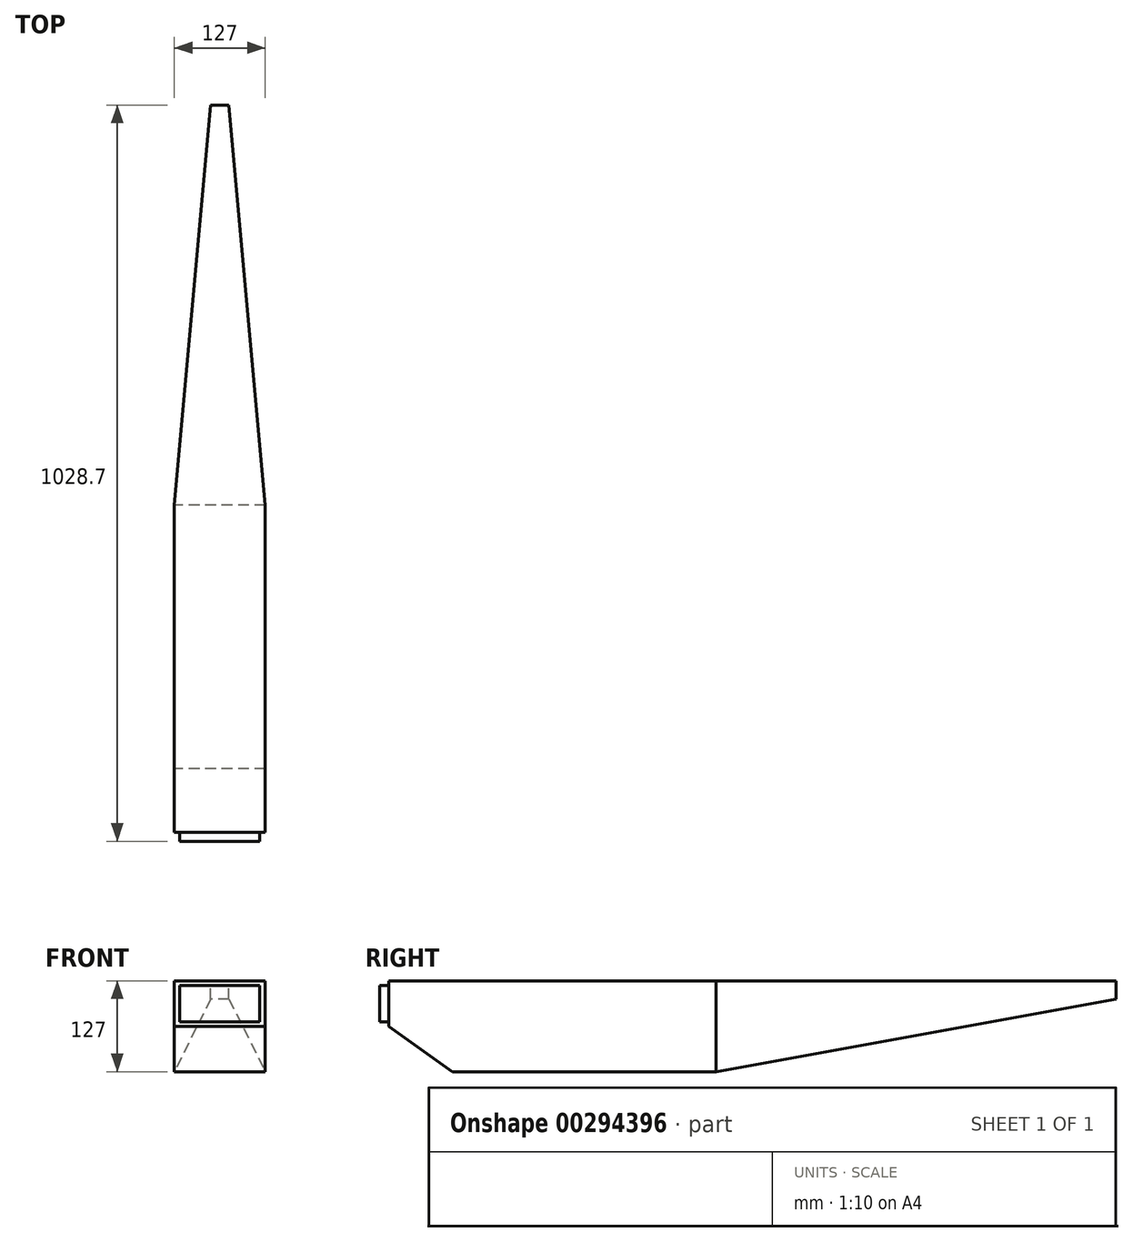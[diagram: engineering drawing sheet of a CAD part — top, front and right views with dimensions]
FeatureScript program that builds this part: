
annotation { "Feature Type Name" : "Feature", "Feature Type Description" : "" }
export const myFeature = defineFeature(function(context is Context, id is Id, definition is map)
    precondition{}
    {
        {
            var Q0;
            Q0=qCreatedBy(makeId("Right.planeOp"),FACE);
            var sketch = newSketch(context, id + "F0", { "sketchPlane" : qUnion([Q0])});
            skLineSegment(sketch, "E0.bottom", {"start": v(-949.91, 104.8) * mm, "end": v(66.09, 104.8) * mm});
            skLineSegment(sketch, "E0.top", {"start": v(-861.01, -22.2) * mm, "end": v(-492.71, -22.2) * mm});
            skLineSegment(sketch, "E0.left", {"start": v(-949.91, 104.8) * mm, "end": v(-949.91, 41.3) * mm});
            skLineSegment(sketch, "E0.right", {"start": v(66.09, 104.8) * mm, "end": v(66.09, 79.4) * mm});
            skPoint(sketch, "E1", {"position": v(66.09, 79.4) * mm});
            skPoint(sketch, "E2", {"position": v(-492.71, -22.2) * mm});
            skLineSegment(sketch, "E3", {"start": v(-492.71, -22.2) * mm, "end": v(66.09, 79.4) * mm});
            skPoint(sketch, "E4.orphan", {"position": v(66.09, -22.2) * mm});
            skPoint(sketch, "E5", {"position": v(-861.01, -22.2) * mm});
            skLineSegment(sketch, "E6", {"start": v(-949.91, 41.3) * mm, "end": v(-861.01, -22.2) * mm});
            skPoint(sketch, "E7.orphan", {"position": v(-949.91, -22.2) * mm});
            skSolve(sketch);
        }
        {
            var Q0;
            Q0 = qSketchRegion(id + "F0", true);
            extrude(context, id + "F1", {"entities" : qUnion([Q0]), "depth" : 127 * mm, "offsetDistance" : 25.4 * mm});
        }
        {
            var Q0;
            Q0=makeQuery(id+"F1.opExtrude","SWEPT_FACE",FACE,{"disambiguationData":[OSD([sQuery(id+"F0.wireOp",EDGE,"E0.left")])]});
            var sketch = newSketch(context, id + "F2", { "sketchPlane" : qUnion([Q0])});
            skLineSegment(sketch, "E8.bottom", {"start": v(7.4, 98.44) * mm, "end": v(119.16, 98.44) * mm});
            skLineSegment(sketch, "E8.top", {"start": v(7.4, 47.64) * mm, "end": v(119.16, 47.64) * mm});
            skLineSegment(sketch, "E8.left", {"start": v(7.4, 98.44) * mm, "end": v(7.4, 47.64) * mm});
            skLineSegment(sketch, "E8.right", {"start": v(119.16, 98.44) * mm, "end": v(119.16, 47.64) * mm});
            skSolve(sketch);
        }
        {
            var Q0;
            Q0 = qSketchRegion(id + "F2", true);
            extrude(context, id + "F3", {"entities" : qUnion([Q0]), "operationType" : NewBodyOperationType.ADD, "depth" : 12.7 * mm, "offsetDistance" : 25.4 * mm});
        }
        {
            var Q0;
            Q0=makeQuery(id+"F1.opExtrude","SWEPT_FACE",FACE,{"disambiguationData":[OSD([sQuery(id+"F0.wireOp",EDGE,"E0.bottom")])]});
            var sketch = newSketch(context, id + "F4", { "sketchPlane" : qUnion([Q0])});
            skPoint(sketch, "E9", {"position": v(127, -492.71) * mm});
            skPoint(sketch, "E10", {"position": v(63.5, 66.09) * mm});
            skPoint(sketch, "E11", {"position": v(76.2, 66.09) * mm});
            skPoint(sketch, "E12", {"position": v(50.8, 66.09) * mm});
            skPoint(sketch, "E13", {"position": v(0, -492.71) * mm});
            skLineSegment(sketch, "E14", {"start": v(50.8, 66.09) * mm, "end": v(0, -492.71) * mm});
            skLineSegment(sketch, "E15", {"start": v(76.2, 66.09) * mm, "end": v(127, -492.71) * mm});
            skLineSegment(sketch, "E16", {"start": v(127, 66.09) * mm, "end": v(76.2, 66.09) * mm});
            skLineSegment(sketch, "E17", {"start": v(0, 66.09) * mm, "end": v(0, -492.71) * mm});
            skLineSegment(sketch, "E18.trimOffspring", {"start": v(50.8, 66.09) * mm, "end": v(0, 66.09) * mm});
            skSolve(sketch);
        }
        {
            var Q0;
            Q0=makeQuery(id+"F4.imprint","IMPRINT",FACE,{"disambiguationData":[TD([[makeQuery(id+"F4.imprint","IMPRINT",EDGE,{"derivedFrom":sQuery(id+"F4.wireOp",EDGE,"E14")}),-1.0]])]});
            var Q1;
            {var subQ0=sQuery(id+"F4.wireOp",EDGE,"E15");Q1=makeQuery(id+"F4.imprint","IMPRINT",FACE,{"disambiguationData":[TD([[makeQuery(id+"F4.imprint","IMPRINT",EDGE,{"derivedFrom":subQ0}),1.0]])]});}
            extrude(context, id + "F5", {"entities" : qUnion([Q0, Q1]), "operationType" : NewBodyOperationType.REMOVE, "oppositeDirection" : true, "depth" : 138.68 * mm, "offsetDistance" : 25.4 * mm});
        }
    });
